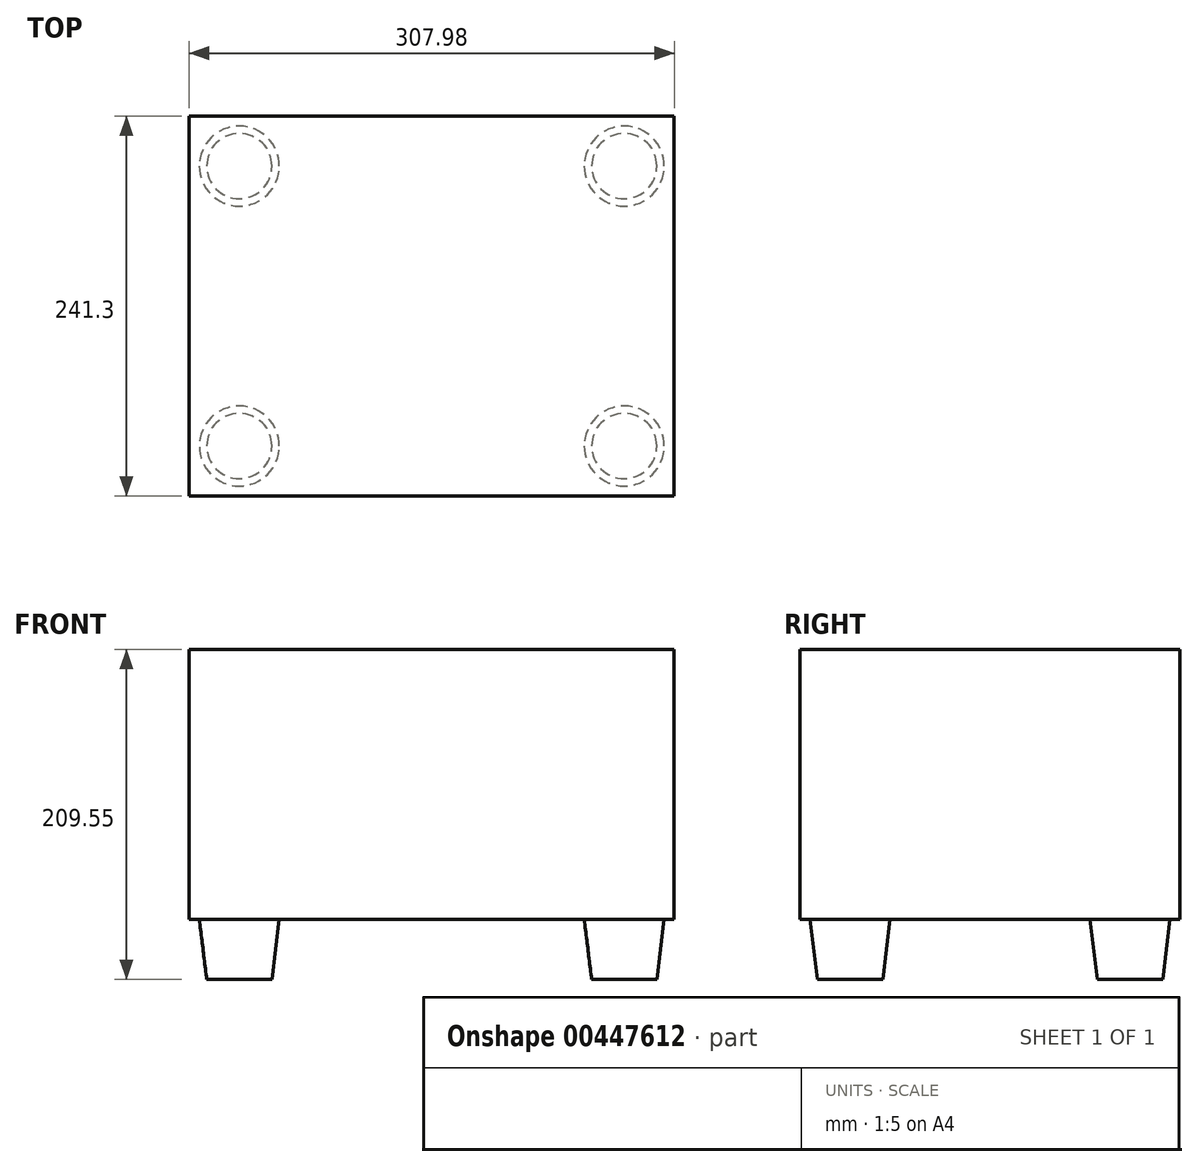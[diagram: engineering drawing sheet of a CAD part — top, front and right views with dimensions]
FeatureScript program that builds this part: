
annotation { "Feature Type Name" : "Feature", "Feature Type Description" : "" }
export const myFeature = defineFeature(function(context is Context, id is Id, definition is map)
    precondition{}
    {
        {
            var Q0;
            Q0=qCreatedBy(makeId("Front.planeOp"),FACE);
            var sketch = newSketch(context, id + "F0", { "sketchPlane" : qUnion([Q0])});
            skLineSegment(sketch, "E0.bottom", {"start": v(0, 0) * mm, "end": v(307.98, 0) * mm});
            skLineSegment(sketch, "E0.top", {"start": v(0, 171.45) * mm, "end": v(307.98, 171.45) * mm});
            skLineSegment(sketch, "E0.left", {"start": v(0, 0) * mm, "end": v(0, 171.45) * mm});
            skLineSegment(sketch, "E0.right", {"start": v(307.98, 0) * mm, "end": v(307.98, 171.45) * mm});
            skSolve(sketch);
        }
        {
            var Q0;
            Q0 = qSketchRegion(id + "F0", true);
            extrude(context, id + "F1", {"entities" : qUnion([Q0]), "depth" : 241.3 * mm});
        }
        {
            var Q0;
            Q0=makeQuery(id+"F1.opExtrude","SWEPT_FACE",FACE,{"disambiguationData":[OSD([sQuery(id+"F0.wireOp",EDGE,"E0.bottom")])]});
            var sketch = newSketch(context, id + "F2", { "sketchPlane" : qUnion([Q0])});
            skCircle(sketch, "E1", {"center": v(31.75, 209.55) * mm, "radius": 25.4 * mm});
            skCircle(sketch, "E2", {"center": v(276.23, 209.55) * mm, "radius": 25.4 * mm});
            skCircle(sketch, "E3", {"center": v(276.23, 31.75) * mm, "radius": 25.4 * mm});
            skCircle(sketch, "E4", {"center": v(31.75, 31.75) * mm, "radius": 25.4 * mm});
            skSolve(sketch);
        }
        {
            var Q0;
            Q0 = qSketchRegion(id + "F2", true);
            extrude(context, id + "F3", {"entities" : qUnion([Q0]), "operationType" : NewBodyOperationType.ADD, "depth" : 38.1 * mm, "hasDraft" : true, "draftAngle" : 7 * degree, "draftPullDirection" : true});
        }
    });
